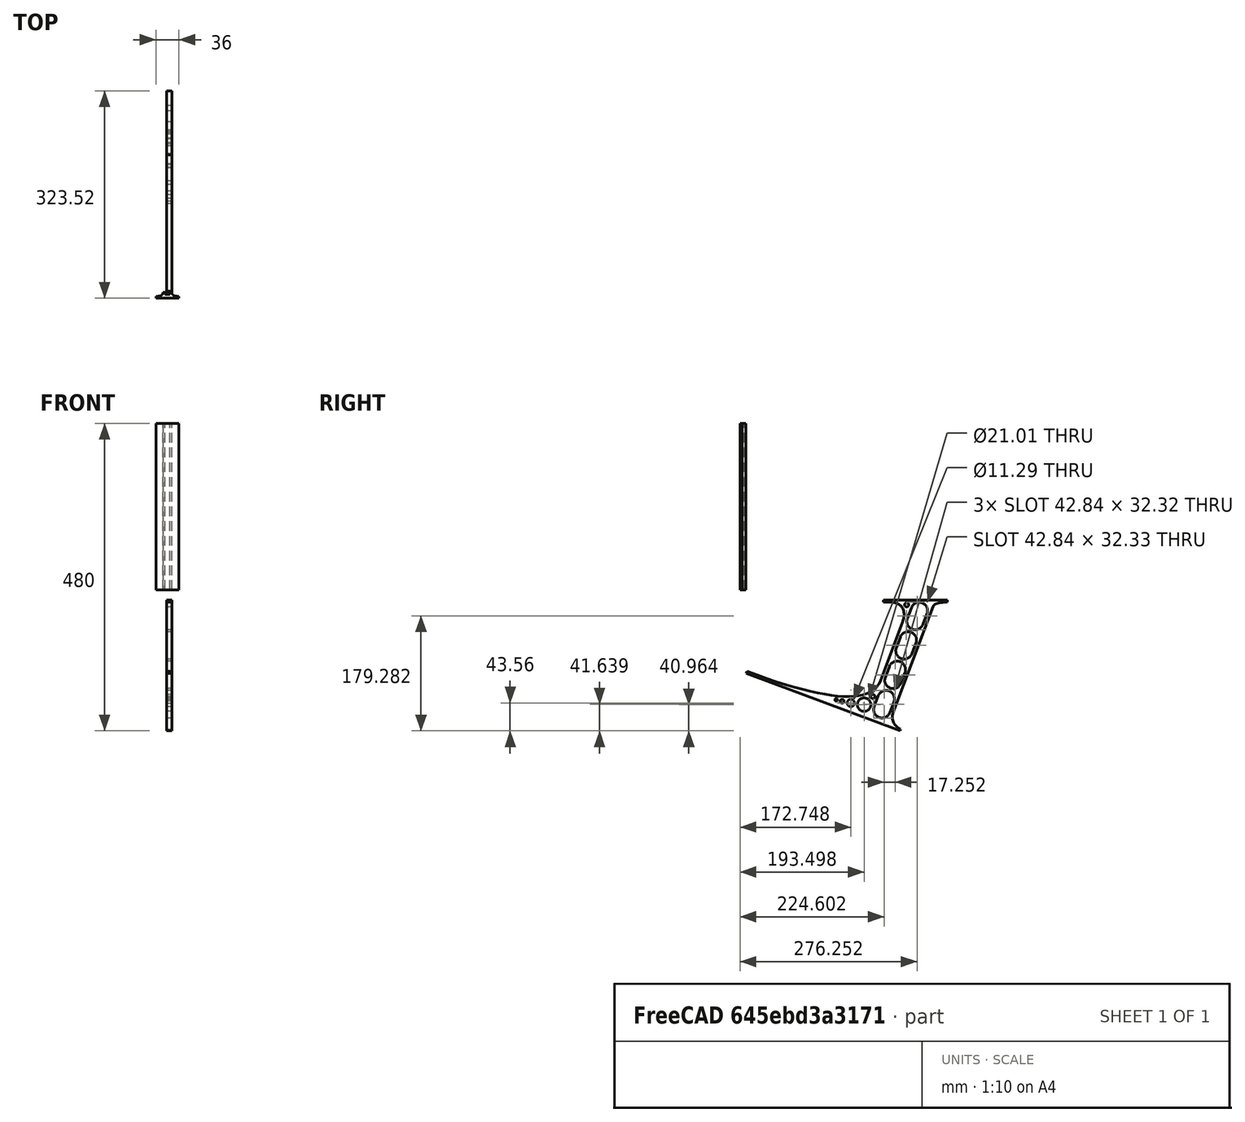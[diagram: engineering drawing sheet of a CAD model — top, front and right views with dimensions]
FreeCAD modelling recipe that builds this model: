
FCSTD DOCUMENT  (FreeCAD 0.19R0.19.2)
Label: laptopStand118FCStd
License: All rights reserved
LicenseURL: http://en.wikipedia.org/wiki/All_rights_reserved
objects: Sketcher::SketchObject×3, Part::Extrusion×3
note: 6 computed .brp shape members not serialized (recipe doc carries the construction recipe); baked Part::Feature solids carry a one-line shape summary decoded from their .brp

FEATURE [Sketcher::SketchObject] Sketch
  FullyConstrained = true
  sketch-geometry (329):
    g0: LineSegment StartX=-10.9272 StartY=-82.7794 StartZ=0 EndX=46.0728 EndY=-51.4823 EndZ=0
    g1: LineSegment StartX=-10.9272 StartY=77.3346 StartZ=0 EndX=-10.9272 EndY=-82.7794 EndZ=0
    g2: LineSegment StartX=-1.92719 StartY=-91.7794 StartZ=0 EndX=46.0728 EndY=-91.7794 EndZ=0
    g3: LineSegment StartX=46.0728 StartY=-65.424 StartZ=0 EndX=-1.92719 EndY=-91.7794 EndZ=0
    g4: LineSegment StartX=46.0728 StartY=-65.424 StartZ=0 EndX=46.0728 EndY=-91.7794 EndZ=0
    g5: LineSegment StartX=46.0728 StartY=77.3346 StartZ=0 EndX=46.0728 EndY=-51.4823 EndZ=0
    g6: LineSegment StartX=-42.9272 StartY=136.221 StartZ=0 EndX=-42.9272 EndY=-103.779 EndZ=0
    g7: LineSegment StartX=407.073 StartY=136.221 StartZ=0 EndX=407.073 EndY=-103.779 EndZ=0
    g8: ArcOfCircle CenterX=-26.9272 CenterY=22.1087 CenterZ=0 NormalX=0 NormalY=0 NormalZ=1 AngleXU=0 Radius=8 StartAngle=1e-16 EndAngle=3.14159
    g9: ArcOfCircle CenterX=-26.9272 CenterY=-83.7794 CenterZ=0 NormalX=0 NormalY=0 NormalZ=1 AngleXU=0 Radius=8 StartAngle=3.14159 EndAngle=6.28319
    g10: LineSegment StartX=-34.9272 StartY=22.1087 StartZ=0 EndX=-34.9272 EndY=-83.7794 EndZ=0
    g11: LineSegment StartX=-18.9272 StartY=22.1087 StartZ=0 EndX=-18.9272 EndY=-83.7794 EndZ=0
    g12: ArcOfCircle CenterX=391.073 CenterY=22.1087 CenterZ=0 NormalX=0 NormalY=0 NormalZ=1 AngleXU=0 Radius=8 StartAngle=-4.4e-15 EndAngle=3.14159
    g13: LineSegment StartX=399.073 StartY=22.1087 StartZ=0 EndX=399.073 EndY=-83.7794 EndZ=0
    g14: LineSegment StartX=383.073 StartY=22.1087 StartZ=0 EndX=383.073 EndY=-83.7794 EndZ=0
    g15: ArcOfCircle CenterX=391.073 CenterY=-83.7794 CenterZ=0 NormalX=0 NormalY=0 NormalZ=1 AngleXU=0 Radius=8 StartAngle=3.14159 EndAngle=6.28319
    g16: Circle CenterX=175.022 CenterY=27.0628 CenterZ=0 NormalX=0 NormalY=0 NormalZ=1 AngleXU=0 Radius=1
    g17: Circle CenterX=179.022 CenterY=24.8665 CenterZ=0 NormalX=0 NormalY=0 NormalZ=1 AngleXU=0 Radius=1
    g18: Circle CenterX=179.022 CenterY=27.0628 CenterZ=0 NormalX=0 NormalY=0 NormalZ=1 AngleXU=0 Radius=1
    g19: BSplineCurve PolesCount=3 KnotsCount=2 Degree=2 IsPeriodic=0
    g20: GeomPoint X=175.022 Y=27.0628 Z=0
    g21: GeomPoint X=179.022 Y=27.0628 Z=0
    g22: Circle CenterX=189.124 CenterY=27.0628 CenterZ=0 NormalX=0 NormalY=0 NormalZ=1 AngleXU=0 Radius=1
    g23: Circle CenterX=185.124 CenterY=24.8665 CenterZ=0 NormalX=0 NormalY=0 NormalZ=1 AngleXU=0 Radius=1
    g24: Circle CenterX=185.124 CenterY=27.0628 CenterZ=0 NormalX=0 NormalY=0 NormalZ=1 AngleXU=0 Radius=1
    g25: BSplineCurve PolesCount=3 KnotsCount=2 Degree=2 IsPeriodic=0
    g26: GeomPoint X=189.124 Y=27.0628 Z=0
    g27: GeomPoint X=185.124 Y=27.0628 Z=0
    g28: Circle CenterX=175.022 CenterY=5.37834 CenterZ=0 NormalX=0 NormalY=0 NormalZ=1 AngleXU=0 Radius=1
    g29: Circle CenterX=179.022 CenterY=7.57463 CenterZ=0 NormalX=0 NormalY=0 NormalZ=1 AngleXU=0 Radius=1
    g30: Circle CenterX=179.022 CenterY=5.34704 CenterZ=0 NormalX=0 NormalY=0 NormalZ=1 AngleXU=0 Radius=1
    g31: BSplineCurve PolesCount=3 KnotsCount=2 Degree=2 IsPeriodic=0
    g32: GeomPoint X=175.022 Y=5.37834 Z=0
    g33: GeomPoint X=179.022 Y=5.34704 Z=0
    g34: Circle CenterX=189.124 CenterY=5.37834 CenterZ=0 NormalX=0 NormalY=0 NormalZ=1 AngleXU=0 Radius=1
    g35: Circle CenterX=185.124 CenterY=7.57463 CenterZ=0 NormalX=0 NormalY=0 NormalZ=1 AngleXU=0 Radius=1
    g36: Circle CenterX=185.124 CenterY=5.34704 CenterZ=0 NormalX=0 NormalY=0 NormalZ=1 AngleXU=0 Radius=1
    g37: BSplineCurve PolesCount=3 KnotsCount=2 Degree=2 IsPeriodic=0
    g38: GeomPoint X=189.124 Y=5.37834 Z=0
    g39: GeomPoint X=185.124 Y=5.34704 Z=0
    g40: Circle CenterX=165.871 CenterY=18.1458 CenterZ=0 NormalX=0 NormalY=0 NormalZ=1 AngleXU=0 Radius=1
    g41: Circle CenterX=169.377 CenterY=16.2206 CenterZ=0 NormalX=0 NormalY=0 NormalZ=1 AngleXU=0 Radius=1
    g42: Circle CenterX=165.871 CenterY=14.2954 CenterZ=0 NormalX=0 NormalY=0 NormalZ=1 AngleXU=0 Radius=1
    g43: BSplineCurve PolesCount=3 KnotsCount=2 Degree=2 IsPeriodic=0
    g44: GeomPoint X=165.871 Y=18.1458 Z=0
    g45: GeomPoint X=165.871 Y=14.2954 Z=0
    g46: Circle CenterX=198.275 CenterY=18.1458 CenterZ=0 NormalX=0 NormalY=0 NormalZ=1 AngleXU=0 Radius=1
    g47: Circle CenterX=194.768 CenterY=16.2206 CenterZ=0 NormalX=0 NormalY=0 NormalZ=1 AngleXU=0 Radius=1
    g48: Circle CenterX=198.275 CenterY=14.2954 CenterZ=0 NormalX=0 NormalY=0 NormalZ=1 AngleXU=0 Radius=1
    g49: BSplineCurve PolesCount=3 KnotsCount=2 Degree=2 IsPeriodic=0
    g50: GeomPoint X=198.275 Y=18.1458 Z=0
    g51: GeomPoint X=198.275 Y=14.2954 Z=0
    g52: LineSegment StartX=407.073 StartY=-103.779 StartZ=0 EndX=-42.9272 EndY=-103.779 EndZ=0
    g53: LineSegment StartX=407.073 StartY=136.221 StartZ=0 EndX=-42.9272 EndY=136.221 EndZ=0
    g54: LineSegment StartX=46.0728 StartY=77.3346 StartZ=0 EndX=-10.9272 EndY=77.3346 EndZ=0
    g55: Circle CenterX=125.607 CenterY=54.1951 CenterZ=0 NormalX=0 NormalY=0 NormalZ=1 AngleXU=0 Radius=1
    g56: Circle CenterX=139.632 CenterY=46.4944 CenterZ=0 NormalX=0 NormalY=0 NormalZ=1 AngleXU=0 Radius=1
    g57: Circle CenterX=127.326 CenterY=56.7187 CenterZ=0 NormalX=0 NormalY=0 NormalZ=1 AngleXU=0 Radius=1
    g58: BSplineCurve PolesCount=3 KnotsCount=2 Degree=2 IsPeriodic=0
    g59: GeomPoint X=125.607 Y=54.1951 Z=0
    g60: GeomPoint X=127.326 Y=56.7187 Z=0
    g61: Circle CenterX=236.821 CenterY=56.7187 CenterZ=0 NormalX=0 NormalY=0 NormalZ=1 AngleXU=0 Radius=1
    g62: Circle CenterX=224.513 CenterY=46.4944 CenterZ=0 NormalX=0 NormalY=0 NormalZ=1 AngleXU=0 Radius=1
    g63: Circle CenterX=238.538 CenterY=54.1951 CenterZ=0 NormalX=0 NormalY=0 NormalZ=1 AngleXU=0 Radius=1
    g64: BSplineCurve PolesCount=3 KnotsCount=2 Degree=2 IsPeriodic=0
    g65: GeomPoint X=236.821 Y=56.7187 Z=0
    g66: GeomPoint X=238.538 Y=54.1951 Z=0
    g67: Circle CenterX=238.538 CenterY=-21.7539 CenterZ=0 NormalX=0 NormalY=0 NormalZ=1 AngleXU=0 Radius=1
    g68: Circle CenterX=224.513 CenterY=-14.0532 CenterZ=0 NormalX=0 NormalY=0 NormalZ=1 AngleXU=0 Radius=1
    g69: Circle CenterX=236.821 CenterY=-24.2775 CenterZ=0 NormalX=0 NormalY=0 NormalZ=1 AngleXU=0 Radius=1
    g70: BSplineCurve PolesCount=3 KnotsCount=2 Degree=2 IsPeriodic=0
    g71: GeomPoint X=238.538 Y=-21.7539 Z=0
    g72: GeomPoint X=236.821 Y=-24.2775 Z=0
    g73: Circle CenterX=125.607 CenterY=-21.7539 CenterZ=0 NormalX=0 NormalY=0 NormalZ=1 AngleXU=0 Radius=1
    g74: Circle CenterX=139.632 CenterY=-14.0532 CenterZ=0 NormalX=0 NormalY=0 NormalZ=1 AngleXU=0 Radius=1
    g75: Circle CenterX=127.325 CenterY=-24.2775 CenterZ=0 NormalX=0 NormalY=0 NormalZ=1 AngleXU=0 Radius=1
    g76: BSplineCurve PolesCount=3 KnotsCount=2 Degree=2 IsPeriodic=0
    g77: GeomPoint X=125.607 Y=-21.7539 Z=0
    g78: GeomPoint X=127.325 Y=-24.2775 Z=0
    g79: Circle CenterX=302.996 CenterY=111.695 CenterZ=0 NormalX=0 NormalY=0 NormalZ=1 AngleXU=0 Radius=1
    g80: Circle CenterX=306.073 CenterY=114.251 CenterZ=0 NormalX=0 NormalY=0 NormalZ=1 AngleXU=0 Radius=1
    g81: Circle CenterX=306.073 CenterY=110.251 CenterZ=0 NormalX=0 NormalY=0 NormalZ=1 AngleXU=0 Radius=1
    g82: BSplineCurve PolesCount=3 KnotsCount=2 Degree=2 IsPeriodic=0
    g83: GeomPoint X=302.996 Y=111.695 Z=0
    g84: GeomPoint X=306.073 Y=110.251 Z=0
    g85: Circle CenterX=306.073 CenterY=95.2763 CenterZ=0 NormalX=0 NormalY=0 NormalZ=1 AngleXU=0 Radius=1
    g86: Circle CenterX=306.073 CenterY=91.2763 CenterZ=0 NormalX=0 NormalY=0 NormalZ=1 AngleXU=0 Radius=1
    g87: Circle CenterX=302.567 CenterY=89.3511 CenterZ=0 NormalX=0 NormalY=0 NormalZ=1 AngleXU=0 Radius=1
    g88: BSplineCurve PolesCount=3 KnotsCount=2 Degree=2 IsPeriodic=0
    g89: GeomPoint X=306.073 Y=95.2763 Z=0
    g90: GeomPoint X=302.567 Y=89.3511 Z=0
    g91: LineSegment StartX=306.073 StartY=110.251 StartZ=0 EndX=306.073 EndY=95.2763 EndZ=0
    g92: LineSegment StartX=302.996 StartY=111.695 StartZ=0 EndX=236.821 EndY=56.7187 EndZ=0
    g93: LineSegment StartX=238.538 StartY=54.1951 StartZ=0 EndX=302.567 EndY=89.3511 EndZ=0
    g94: Circle CenterX=61.1496 CenterY=111.695 CenterZ=0 NormalX=0 NormalY=0 NormalZ=1 AngleXU=0 Radius=1
    g95: Circle CenterX=58.0728 CenterY=114.251 CenterZ=0 NormalX=0 NormalY=0 NormalZ=1 AngleXU=0 Radius=1
    g96: Circle CenterX=58.0728 CenterY=110.251 CenterZ=0 NormalX=0 NormalY=0 NormalZ=1 AngleXU=0 Radius=1
    g97: BSplineCurve PolesCount=3 KnotsCount=2 Degree=2 IsPeriodic=0
    g98: GeomPoint X=61.1496 Y=111.695 Z=0
    g99: GeomPoint X=58.0728 Y=110.251 Z=0
    g100: Circle CenterX=61.5791 CenterY=89.3511 CenterZ=0 NormalX=0 NormalY=0 NormalZ=1 AngleXU=0 Radius=1
    g101: Circle CenterX=58.0728 CenterY=91.2763 CenterZ=0 NormalX=0 NormalY=0 NormalZ=1 AngleXU=0 Radius=1
    g102: Circle CenterX=58.0728 CenterY=95.2763 CenterZ=0 NormalX=0 NormalY=0 NormalZ=1 AngleXU=0 Radius=1
    g103: BSplineCurve PolesCount=3 KnotsCount=2 Degree=2 IsPeriodic=0
    g104: GeomPoint X=61.5791 Y=89.3511 Z=0
    g105: GeomPoint X=58.0728 Y=95.2763 Z=0
    g106: LineSegment StartX=58.0728 StartY=110.251 StartZ=0 EndX=58.0728 EndY=95.2763 EndZ=0
    g107: LineSegment StartX=61.1496 StartY=111.695 StartZ=0 EndX=127.326 EndY=56.7187 EndZ=0
    g108: LineSegment StartX=125.607 StartY=54.1951 StartZ=0 EndX=61.5791 EndY=89.3511 EndZ=0
    g109: Circle CenterX=61.5791 CenterY=-56.9099 CenterZ=0 NormalX=0 NormalY=0 NormalZ=1 AngleXU=0 Radius=1
    g110: Circle CenterX=58.0728 CenterY=-58.8351 CenterZ=0 NormalX=0 NormalY=0 NormalZ=1 AngleXU=0 Radius=1
    g111: Circle CenterX=58.0728 CenterY=-62.8351 CenterZ=0 NormalX=0 NormalY=0 NormalZ=1 AngleXU=0 Radius=1
    g112: BSplineCurve PolesCount=3 KnotsCount=2 Degree=2 IsPeriodic=0
    g113: GeomPoint X=61.5791 Y=-56.9099 Z=0
    g114: GeomPoint X=58.0728 Y=-62.8351 Z=0
    g115: Circle CenterX=58.0728 CenterY=-77.8102 CenterZ=0 NormalX=0 NormalY=0 NormalZ=1 AngleXU=0 Radius=1
    g116: Circle CenterX=58.0728 CenterY=-81.8102 CenterZ=0 NormalX=0 NormalY=0 NormalZ=1 AngleXU=0 Radius=1
    g117: Circle CenterX=61.1496 CenterY=-79.2541 CenterZ=0 NormalX=0 NormalY=0 NormalZ=1 AngleXU=0 Radius=1
    g118: BSplineCurve PolesCount=3 KnotsCount=2 Degree=2 IsPeriodic=0
    g119: GeomPoint X=58.0728 Y=-77.8102 Z=0
    g120: GeomPoint X=61.1496 Y=-79.2541 Z=0
    g121: LineSegment StartX=58.0728 StartY=-62.8351 StartZ=0 EndX=58.0728 EndY=-77.8102 EndZ=0
    g122: LineSegment StartX=61.1496 StartY=-79.2541 StartZ=0 EndX=127.325 EndY=-24.2775 EndZ=0
    g123: LineSegment StartX=125.607 StartY=-21.7539 StartZ=0 EndX=61.5791 EndY=-56.9099 EndZ=0
    g124: Circle CenterX=302.567 CenterY=-56.9099 CenterZ=0 NormalX=0 NormalY=0 NormalZ=1 AngleXU=0 Radius=1
    g125: Circle CenterX=306.073 CenterY=-58.8351 CenterZ=0 NormalX=0 NormalY=0 NormalZ=1 AngleXU=0 Radius=1
    g126: Circle CenterX=306.073 CenterY=-62.8351 CenterZ=0 NormalX=0 NormalY=0 NormalZ=1 AngleXU=0 Radius=1
    g127: BSplineCurve PolesCount=3 KnotsCount=2 Degree=2 IsPeriodic=0
    g128: GeomPoint X=302.567 Y=-56.9099 Z=0
    g129: GeomPoint X=306.073 Y=-62.8351 Z=0
    g130: Circle CenterX=302.996 CenterY=-79.2541 CenterZ=0 NormalX=0 NormalY=0 NormalZ=1 AngleXU=0 Radius=1
    g131: Circle CenterX=306.073 CenterY=-81.8102 CenterZ=0 NormalX=0 NormalY=0 NormalZ=1 AngleXU=0 Radius=1
    g132: Circle CenterX=306.073 CenterY=-77.8102 CenterZ=0 NormalX=0 NormalY=0 NormalZ=1 AngleXU=0 Radius=1
    g133: BSplineCurve PolesCount=3 KnotsCount=2 Degree=2 IsPeriodic=0
    g134: GeomPoint X=302.996 Y=-79.2541 Z=0
    g135: GeomPoint X=306.073 Y=-77.8102 Z=0
    g136: LineSegment StartX=306.073 StartY=-62.8351 StartZ=0 EndX=306.073 EndY=-77.8102 EndZ=0
    g137: LineSegment StartX=302.996 StartY=-79.2541 StartZ=0 EndX=236.821 EndY=-24.2775 EndZ=0
    g138: LineSegment StartX=238.538 StartY=-21.7539 StartZ=0 EndX=302.567 EndY=-56.9099 EndZ=0
    g139: Circle CenterX=61.6457 CenterY=-88.8112 CenterZ=0 NormalX=0 NormalY=0 NormalZ=1 AngleXU=0 Radius=1
    g140: Circle CenterX=58.0728 CenterY=-91.7794 CenterZ=0 NormalX=0 NormalY=0 NormalZ=1 AngleXU=0 Radius=1
    g141: Circle CenterX=63.9135 CenterY=-91.7794 CenterZ=0 NormalX=0 NormalY=0 NormalZ=1 AngleXU=0 Radius=1
    g142: BSplineCurve PolesCount=3 KnotsCount=2 Degree=2 IsPeriodic=0
    g143: GeomPoint X=61.6457 Y=-88.8112 Z=0
    g144: GeomPoint X=63.9135 Y=-91.7794 Z=0
    g145: Circle CenterX=179.022 CenterY=-85.8163 CenterZ=0 NormalX=0 NormalY=0 NormalZ=1 AngleXU=0 Radius=1
    g146: Circle CenterX=179.022 CenterY=-91.7794 CenterZ=0 NormalX=0 NormalY=0 NormalZ=1 AngleXU=0 Radius=1
    g147: Circle CenterX=171.895 CenterY=-91.7794 CenterZ=0 NormalX=0 NormalY=0 NormalZ=1 AngleXU=0 Radius=1
    g148: BSplineCurve PolesCount=3 KnotsCount=2 Degree=2 IsPeriodic=0
    g149: GeomPoint X=179.022 Y=-85.8163 Z=0
    g150: GeomPoint X=171.895 Y=-91.7794 Z=0
    g151: Circle CenterX=185.124 CenterY=-86.2028 CenterZ=0 NormalX=0 NormalY=0 NormalZ=1 AngleXU=0 Radius=1
    g152: Circle CenterX=185.124 CenterY=-91.7794 CenterZ=0 NormalX=0 NormalY=0 NormalZ=1 AngleXU=0 Radius=1
    g153: Circle CenterX=191.747 CenterY=-91.7794 CenterZ=0 NormalX=0 NormalY=0 NormalZ=1 AngleXU=0 Radius=1
    g154: BSplineCurve PolesCount=3 KnotsCount=2 Degree=2 IsPeriodic=0
    g155: GeomPoint X=185.124 Y=-86.2028 Z=0
    g156: GeomPoint X=191.747 Y=-91.7794 Z=0
    g157: Circle CenterX=299.888 CenterY=-86.6413 CenterZ=0 NormalX=0 NormalY=0 NormalZ=1 AngleXU=0 Radius=1
    g158: Circle CenterX=306.073 CenterY=-91.7794 CenterZ=0 NormalX=0 NormalY=0 NormalZ=1 AngleXU=0 Radius=1
    g159: Circle CenterX=298.776 CenterY=-91.7794 CenterZ=0 NormalX=0 NormalY=0 NormalZ=1 AngleXU=0 Radius=1
    g160: BSplineCurve PolesCount=3 KnotsCount=2 Degree=2 IsPeriodic=0
    g161: GeomPoint X=299.888 Y=-86.6413 Z=0
    g162: GeomPoint X=298.776 Y=-91.7794 Z=0
    g163: LineSegment StartX=189.124 StartY=5.37834 StartZ=0 EndX=299.888 EndY=-86.6413 EndZ=0
    g164: LineSegment StartX=298.776 StartY=-91.7794 StartZ=0 EndX=191.747 EndY=-91.7794 EndZ=0
    g165: LineSegment StartX=185.124 StartY=-86.2028 StartZ=0 EndX=185.124 EndY=5.34704 EndZ=0
    g166: LineSegment StartX=179.022 StartY=5.34704 StartZ=0 EndX=179.022 EndY=-85.8163 EndZ=0
    g167: LineSegment StartX=171.895 StartY=-91.7794 StartZ=0 EndX=63.9135 EndY=-91.7794 EndZ=0
    g168: LineSegment StartX=61.6457 StartY=-88.8112 StartZ=0 EndX=175.022 EndY=5.37834 EndZ=0
    g169: Circle CenterX=302.073 CenterY=124.221 CenterZ=0 NormalX=0 NormalY=0 NormalZ=1 AngleXU=0 Radius=1
    g170: Circle CenterX=306.073 CenterY=124.221 CenterZ=0 NormalX=0 NormalY=0 NormalZ=1 AngleXU=0 Radius=1
    g171: Circle CenterX=302.996 CenterY=121.665 CenterZ=0 NormalX=0 NormalY=0 NormalZ=1 AngleXU=0 Radius=1
    g172: BSplineCurve PolesCount=3 KnotsCount=2 Degree=2 IsPeriodic=0
    g173: GeomPoint X=302.073 Y=124.221 Z=0
    g174: GeomPoint X=302.996 Y=121.665 Z=0
    g175: Circle CenterX=189.124 CenterY=124.221 CenterZ=0 NormalX=0 NormalY=0 NormalZ=1 AngleXU=0 Radius=1
    g176: Circle CenterX=185.124 CenterY=124.221 CenterZ=0 NormalX=0 NormalY=0 NormalZ=1 AngleXU=0 Radius=1
    g177: Circle CenterX=185.124 CenterY=120.221 CenterZ=0 NormalX=0 NormalY=0 NormalZ=1 AngleXU=0 Radius=1
    g178: BSplineCurve PolesCount=3 KnotsCount=2 Degree=2 IsPeriodic=0
    g179: GeomPoint X=189.124 Y=124.221 Z=0
    g180: GeomPoint X=185.124 Y=120.221 Z=0
    g181: Circle CenterX=175.022 CenterY=124.221 CenterZ=0 NormalX=0 NormalY=0 NormalZ=1 AngleXU=0 Radius=1
    g182: Circle CenterX=179.022 CenterY=124.221 CenterZ=0 NormalX=0 NormalY=0 NormalZ=1 AngleXU=0 Radius=1
    g183: Circle CenterX=179.022 CenterY=120.221 CenterZ=0 NormalX=0 NormalY=0 NormalZ=1 AngleXU=0 Radius=1
    g184: BSplineCurve PolesCount=3 KnotsCount=2 Degree=2 IsPeriodic=0
    g185: GeomPoint X=175.022 Y=124.221 Z=0
    g186: GeomPoint X=179.022 Y=120.221 Z=0
    g187: Circle CenterX=62.0728 CenterY=124.221 CenterZ=0 NormalX=0 NormalY=0 NormalZ=1 AngleXU=0 Radius=1
    g188: Circle CenterX=58.0728 CenterY=124.221 CenterZ=0 NormalX=0 NormalY=0 NormalZ=1 AngleXU=0 Radius=1
    g189: Circle CenterX=61.1496 CenterY=121.665 CenterZ=0 NormalX=0 NormalY=0 NormalZ=1 AngleXU=0 Radius=1
    g190: BSplineCurve PolesCount=3 KnotsCount=2 Degree=2 IsPeriodic=0
    g191: GeomPoint X=62.0728 Y=124.221 Z=0
    g192: GeomPoint X=61.1496 Y=121.665 Z=0
    g193: LineSegment StartX=62.0728 StartY=124.221 StartZ=0 EndX=175.022 EndY=124.221 EndZ=0
    g194: LineSegment StartX=179.022 StartY=120.221 StartZ=0 EndX=179.022 EndY=27.0628 EndZ=0
    g195: LineSegment StartX=185.124 StartY=27.0628 StartZ=0 EndX=185.124 EndY=120.221 EndZ=0
    g196: LineSegment StartX=189.124 StartY=124.221 StartZ=0 EndX=302.073 EndY=124.221 EndZ=0
    g197: LineSegment StartX=302.996 StartY=121.665 StartZ=0 EndX=189.124 EndY=27.0628 EndZ=0
    g198: LineSegment StartX=175.022 StartY=27.0628 StartZ=0 EndX=61.1496 EndY=121.665 EndZ=0
    g199: Circle CenterX=61.5791 CenterY=75.4095 CenterZ=0 NormalX=0 NormalY=0 NormalZ=1 AngleXU=0 Radius=1
    g200: Circle CenterX=58.0728 CenterY=77.3346 CenterZ=0 NormalX=0 NormalY=0 NormalZ=1 AngleXU=0 Radius=1
    g201: Circle CenterX=58.0728 CenterY=73.3346 CenterZ=0 NormalX=0 NormalY=0 NormalZ=1 AngleXU=0 Radius=1
    g202: BSplineCurve PolesCount=3 KnotsCount=2 Degree=2 IsPeriodic=0
    g203: GeomPoint X=61.5791 Y=75.4095 Z=0
    g204: GeomPoint X=58.0728 Y=73.3346 Z=0
    g205: Circle CenterX=58.0728 CenterY=-40.8935 CenterZ=0 NormalX=0 NormalY=0 NormalZ=1 AngleXU=0 Radius=1
    g206: Circle CenterX=58.0728 CenterY=-44.8935 CenterZ=0 NormalX=0 NormalY=0 NormalZ=1 AngleXU=0 Radius=1
    g207: Circle CenterX=61.5791 CenterY=-42.9683 CenterZ=0 NormalX=0 NormalY=0 NormalZ=1 AngleXU=0 Radius=1
    g208: BSplineCurve PolesCount=3 KnotsCount=2 Degree=2 IsPeriodic=0
    g209: GeomPoint X=58.0728 Y=-40.8935 Z=0
    g210: GeomPoint X=61.5791 Y=-42.9683 Z=0
    g211: LineSegment StartX=61.5791 StartY=-42.9683 StartZ=0 EndX=165.871 EndY=14.2954 EndZ=0
    g212: LineSegment StartX=165.871 StartY=18.1458 StartZ=0 EndX=61.5791 EndY=75.4095 EndZ=0
    g213: LineSegment StartX=58.0728 StartY=73.3346 StartZ=0 EndX=58.0728 EndY=-40.8935 EndZ=0
    g214: Circle CenterX=302.567 CenterY=-42.9683 CenterZ=0 NormalX=0 NormalY=0 NormalZ=1 AngleXU=0 Radius=1
    g215: Circle CenterX=306.073 CenterY=-44.8935 CenterZ=0 NormalX=0 NormalY=0 NormalZ=1 AngleXU=0 Radius=1
    g216: Circle CenterX=306.073 CenterY=-40.8935 CenterZ=0 NormalX=0 NormalY=0 NormalZ=1 AngleXU=0 Radius=1
    g217: BSplineCurve PolesCount=3 KnotsCount=2 Degree=2 IsPeriodic=0
    g218: GeomPoint X=302.567 Y=-42.9683 Z=0
    g219: GeomPoint X=306.073 Y=-40.8935 Z=0
    g220: Circle CenterX=306.073 CenterY=73.3346 CenterZ=0 NormalX=0 NormalY=0 NormalZ=1 AngleXU=0 Radius=1
    g221: Circle CenterX=306.073 CenterY=77.3346 CenterZ=0 NormalX=0 NormalY=0 NormalZ=1 AngleXU=0 Radius=1
    g222: Circle CenterX=302.567 CenterY=75.4095 CenterZ=0 NormalX=0 NormalY=0 NormalZ=1 AngleXU=0 Radius=1
    g223: BSplineCurve PolesCount=3 KnotsCount=2 Degree=2 IsPeriodic=0
    g224: GeomPoint X=306.073 Y=73.3346 Z=0
    g225: GeomPoint X=302.567 Y=75.4095 Z=0
    g226: LineSegment StartX=302.567 StartY=-42.9683 StartZ=0 EndX=198.275 EndY=14.2954 EndZ=0
    g227: LineSegment StartX=198.275 StartY=18.1458 StartZ=0 EndX=302.567 EndY=75.4095 EndZ=0
    g228: LineSegment StartX=306.073 StartY=73.3346 StartZ=0 EndX=306.073 EndY=-40.8935 EndZ=0
    g229: LineSegment StartX=322.073 StartY=105.865 StartZ=0 EndX=328.643 EndY=105.865 EndZ=0
    g230: LineSegment StartX=318.073 StartY=120.221 StartZ=0 EndX=318.073 EndY=109.865 EndZ=0
    g231: LineSegment StartX=336.157 StartY=107.779 StartZ=0 EndX=362.567 EndY=122.294 EndZ=0
    g232: Circle CenterX=362.073 CenterY=124.221 CenterZ=0 NormalX=0 NormalY=0 NormalZ=1 AngleXU=0 Radius=1
    g233: Circle CenterX=366.073 CenterY=124.221 CenterZ=0 NormalX=0 NormalY=0 NormalZ=1 AngleXU=0 Radius=1
    g234: Circle CenterX=362.567 CenterY=122.294 CenterZ=0 NormalX=0 NormalY=0 NormalZ=1 AngleXU=0 Radius=1
    g235: BSplineCurve PolesCount=3 KnotsCount=2 Degree=2 IsPeriodic=0
    g236: GeomPoint X=362.073 Y=124.221 Z=0
    g237: GeomPoint X=362.567 Y=122.294 Z=0
    g238: Circle CenterX=322.073 CenterY=124.221 CenterZ=0 NormalX=0 NormalY=0 NormalZ=1 AngleXU=0 Radius=1
    g239: Circle CenterX=318.073 CenterY=124.221 CenterZ=0 NormalX=0 NormalY=0 NormalZ=1 AngleXU=0 Radius=1
    g240: Circle CenterX=318.073 CenterY=120.221 CenterZ=0 NormalX=0 NormalY=0 NormalZ=1 AngleXU=0 Radius=1
    g241: BSplineCurve PolesCount=3 KnotsCount=2 Degree=2 IsPeriodic=0
    g242: GeomPoint X=322.073 Y=124.221 Z=0
    g243: GeomPoint X=318.073 Y=120.221 Z=0
    g244: Circle CenterX=322.073 CenterY=105.865 CenterZ=0 NormalX=0 NormalY=0 NormalZ=1 AngleXU=0 Radius=1
    g245: Circle CenterX=318.073 CenterY=105.865 CenterZ=0 NormalX=0 NormalY=0 NormalZ=1 AngleXU=0 Radius=1
    g246: Circle CenterX=318.073 CenterY=109.865 CenterZ=0 NormalX=0 NormalY=0 NormalZ=1 AngleXU=0 Radius=1
    g247: BSplineCurve PolesCount=3 KnotsCount=2 Degree=2 IsPeriodic=0
    g248: GeomPoint X=322.073 Y=105.865 Z=0
    g249: GeomPoint X=318.073 Y=109.865 Z=0
    g250: Circle CenterX=336.157 CenterY=107.779 CenterZ=0 NormalX=0 NormalY=0 NormalZ=1 AngleXU=0 Radius=1
    g251: Circle CenterX=332.651 CenterY=105.853 CenterZ=0 NormalX=0 NormalY=0 NormalZ=1 AngleXU=0 Radius=1
    g252: Circle CenterX=328.643 CenterY=105.865 CenterZ=0 NormalX=0 NormalY=0 NormalZ=1 AngleXU=0 Radius=1
    g253: BSplineCurve PolesCount=3 KnotsCount=2 Degree=2 IsPeriodic=0
    g254: GeomPoint X=336.157 Y=107.779 Z=0
    g255: GeomPoint X=328.643 Y=105.865 Z=0
    g256: LineSegment StartX=322.073 StartY=124.221 StartZ=0 EndX=362.073 EndY=124.221 EndZ=0
    g257: Circle CenterX=371.567 CenterY=-80.8644 CenterZ=0 NormalX=0 NormalY=0 NormalZ=1 AngleXU=0 Radius=1
    g258: Circle CenterX=375.073 CenterY=-82.7896 CenterZ=0 NormalX=0 NormalY=0 NormalZ=1 AngleXU=0 Radius=1
    g259: Circle CenterX=375.073 CenterY=-78.7896 CenterZ=0 NormalX=0 NormalY=0 NormalZ=1 AngleXU=0 Radius=1
    g260: BSplineCurve PolesCount=3 KnotsCount=2 Degree=2 IsPeriodic=0
    g261: GeomPoint X=371.567 Y=-80.8644 Z=0
    g262: GeomPoint X=375.073 Y=-78.7896 Z=0
    g263: Circle CenterX=321.579 CenterY=-53.4075 CenterZ=0 NormalX=0 NormalY=0 NormalZ=1 AngleXU=0 Radius=1
    g264: Circle CenterX=318.073 CenterY=-51.4823 CenterZ=0 NormalX=0 NormalY=0 NormalZ=1 AngleXU=0 Radius=1
    g265: Circle CenterX=318.073 CenterY=-47.4823 CenterZ=0 NormalX=0 NormalY=0 NormalZ=1 AngleXU=0 Radius=1
    g266: BSplineCurve PolesCount=3 KnotsCount=2 Degree=2 IsPeriodic=0
    g267: GeomPoint X=321.579 Y=-53.4075 Z=0
    g268: GeomPoint X=318.073 Y=-47.4823 Z=0
    g269: Circle CenterX=318.073 CenterY=79.9235 CenterZ=0 NormalX=0 NormalY=0 NormalZ=1 AngleXU=0 Radius=1
    g270: Circle CenterX=318.073 CenterY=83.9235 CenterZ=0 NormalX=0 NormalY=0 NormalZ=1 AngleXU=0 Radius=1
    g271: Circle CenterX=322.073 CenterY=83.9235 CenterZ=0 NormalX=0 NormalY=0 NormalZ=1 AngleXU=0 Radius=1
    g272: BSplineCurve PolesCount=3 KnotsCount=2 Degree=2 IsPeriodic=0
    g273: GeomPoint X=318.073 Y=79.9235 Z=0
    g274: GeomPoint X=322.073 Y=83.9235 Z=0
    g275: Circle CenterX=375.073 CenterY=79.9235 CenterZ=0 NormalX=0 NormalY=0 NormalZ=1 AngleXU=0 Radius=1
    g276: Circle CenterX=375.073 CenterY=83.9235 CenterZ=0 NormalX=0 NormalY=0 NormalZ=1 AngleXU=0 Radius=1
    g277: Circle CenterX=371.073 CenterY=83.9235 CenterZ=0 NormalX=0 NormalY=0 NormalZ=1 AngleXU=0 Radius=1
    g278: BSplineCurve PolesCount=3 KnotsCount=2 Degree=2 IsPeriodic=0
    g279: GeomPoint X=375.073 Y=79.9235 Z=0
    g280: GeomPoint X=371.073 Y=83.9235 Z=0
    g281: LineSegment StartX=322.073 StartY=83.9235 StartZ=0 EndX=371.073 EndY=83.9235 EndZ=0
    g282: LineSegment StartX=375.073 StartY=79.9235 StartZ=0 EndX=375.073 EndY=-78.7896 EndZ=0
    g283: LineSegment StartX=371.567 StartY=-80.8644 StartZ=0 EndX=321.579 EndY=-53.4075 EndZ=0
    g284: LineSegment StartX=318.073 StartY=-47.4823 StartZ=0 EndX=318.073 EndY=79.9235 EndZ=0
    g285: Circle CenterX=321.579 CenterY=-67.3492 CenterZ=0 NormalX=0 NormalY=0 NormalZ=1 AngleXU=0 Radius=1
    g286: Circle CenterX=318.073 CenterY=-65.424 CenterZ=0 NormalX=0 NormalY=0 NormalZ=1 AngleXU=0 Radius=1
    g287: Circle CenterX=318.073 CenterY=-69.424 CenterZ=0 NormalX=0 NormalY=0 NormalZ=1 AngleXU=0 Radius=1
    g288: BSplineCurve PolesCount=3 KnotsCount=2 Degree=2 IsPeriodic=0
    g289: GeomPoint X=321.579 Y=-67.3492 Z=0
    g290: GeomPoint X=318.073 Y=-69.424 Z=0
    g291: Circle CenterX=362.567 CenterY=-89.8542 CenterZ=0 NormalX=0 NormalY=0 NormalZ=1 AngleXU=0 Radius=1
    g292: Circle CenterX=366.073 CenterY=-91.7794 CenterZ=0 NormalX=0 NormalY=0 NormalZ=1 AngleXU=0 Radius=1
    g293: Circle CenterX=362.073 CenterY=-91.7794 CenterZ=0 NormalX=0 NormalY=0 NormalZ=1 AngleXU=0 Radius=1
    g294: BSplineCurve PolesCount=3 KnotsCount=2 Degree=2 IsPeriodic=0
    g295: GeomPoint X=362.567 Y=-89.8542 Z=0
    g296: GeomPoint X=362.073 Y=-91.7794 Z=0
    g297: Circle CenterX=322.073 CenterY=-91.7794 CenterZ=0 NormalX=0 NormalY=0 NormalZ=1 AngleXU=0 Radius=1
    g298: Circle CenterX=318.073 CenterY=-91.7794 CenterZ=0 NormalX=0 NormalY=0 NormalZ=1 AngleXU=0 Radius=1
    g299: Circle CenterX=318.073 CenterY=-87.7794 CenterZ=0 NormalX=0 NormalY=0 NormalZ=1 AngleXU=0 Radius=1
    g300: BSplineCurve PolesCount=3 KnotsCount=2 Degree=2 IsPeriodic=0
    g301: GeomPoint X=322.073 Y=-91.7794 Z=0
    g302: GeomPoint X=318.073 Y=-87.7794 Z=0
    g303: LineSegment StartX=362.567 StartY=-89.8542 StartZ=0 EndX=321.579 EndY=-67.3492 EndZ=0
    g304: LineSegment StartX=318.073 StartY=-69.424 StartZ=0 EndX=318.073 EndY=-87.7794 EndZ=0
    g305: LineSegment StartX=322.073 StartY=-91.7794 StartZ=0 EndX=362.073 EndY=-91.7794 EndZ=0
    g306: Circle CenterX=2.07281 CenterY=124.221 CenterZ=0 NormalX=0 NormalY=0 NormalZ=1 AngleXU=0 Radius=1
    g307: Circle CenterX=1.57905 CenterY=122.295 CenterZ=0 NormalX=0 NormalY=0 NormalZ=1 AngleXU=0 Radius=1
    g308: BSplineCurve PolesCount=3 KnotsCount=2 Degree=2 IsPeriodic=0
    g309: GeomPoint X=2.07281 Y=124.221 Z=0
    g310: GeomPoint X=1.57905 Y=122.295 Z=0
    g311: Circle CenterX=42.0728 CenterY=124.221 CenterZ=0 NormalX=0 NormalY=0 NormalZ=1 AngleXU=0 Radius=1
    g312: Circle CenterX=46.0728 CenterY=124.221 CenterZ=0 NormalX=0 NormalY=0 NormalZ=1 AngleXU=0 Radius=1
    g313: Circle CenterX=46.0728 CenterY=120.221 CenterZ=0 NormalX=0 NormalY=0 NormalZ=1 AngleXU=0 Radius=1
    g314: BSplineCurve PolesCount=3 KnotsCount=2 Degree=2 IsPeriodic=0
    g315: GeomPoint X=42.0728 Y=124.221 Z=0
    g316: GeomPoint X=46.0728 Y=120.221 Z=0
    g317: Circle CenterX=46.0728 CenterY=109.865 CenterZ=0 NormalX=0 NormalY=0 NormalZ=1 AngleXU=0 Radius=1
    g318: Circle CenterX=46.0728 CenterY=105.865 CenterZ=0 NormalX=0 NormalY=0 NormalZ=1 AngleXU=0 Radius=1
    g319: Circle CenterX=42.0728 CenterY=105.865 CenterZ=0 NormalX=0 NormalY=0 NormalZ=1 AngleXU=0 Radius=1
    g320: BSplineCurve PolesCount=3 KnotsCount=2 Degree=2 IsPeriodic=0
    g321: GeomPoint X=46.0728 Y=109.865 Z=0
    g322: GeomPoint X=42.0728 Y=105.865 Z=0
    g323: Circle CenterX=35.5028 CenterY=105.865 CenterZ=0 NormalX=0 NormalY=0 NormalZ=1 AngleXU=0 Radius=1
    g324: Circle CenterX=31.5028 CenterY=105.865 CenterZ=0 NormalX=0 NormalY=0 NormalZ=1 AngleXU=0 Radius=1
    g325: Circle CenterX=27.9965 CenterY=107.79 CenterZ=0 NormalX=0 NormalY=0 NormalZ=1 AngleXU=0 Radius=1
    g326: BSplineCurve PolesCount=3 KnotsCount=2 Degree=2 IsPeriodic=0
    g327: GeomPoint X=35.5028 Y=105.865 Z=0
    g328: GeomPoint X=27.9965 Y=107.79 Z=0
  constraints (541):
    c: Horizontal(g2)
    c: Coincident(g4,g3)
    c: Coincident(g0,g5)
    c: Block(g4)
    c: Block(g3)
    c: Block(g0)
    c: Block(g1)
    c: Block(g2)
    c: Vertical(g6)
    c: Vertical(g7)
    c: Block(g7)
    c: Block(g6)
    c: Tangent(g8,g11) = 1.5708
    c: Tangent(g8,g10) = -1.5708
    c: Tangent(g10,g9) = -1.5708
    c: Tangent(g11,g9) = 1.5708
    c: Vertical(g10)
    c: Equal(g8,g9)
    c: Block(g11)
    c: Block(g10)
    c: Tangent(g12,g13) = 1.5708
    c: Tangent(g13,g15) = 1.5708
    c: Equal(g12,g15)
    c: Coincident(g14,g12)
    c: Coincident(g14,g15)
    c: Block(g13)
    c: Block(g14)
    c: Weight(g16) = 1
    c: Equal(g16,g17)
    c: Equal(g16,g18)
    c: InternalAlignment(g16,g19)
    c: InternalAlignment(g17,g19)
    c: InternalAlignment(g18,g19)
    c: InternalAlignment(g20,g19)
    c: InternalAlignment(g21,g19)
    c: Weight(g22) = 1
    c: Equal(g22,g23)
    c: Equal(g22,g24)
    c: InternalAlignment(g22,g25)
    c: InternalAlignment(g23,g25)
    c: InternalAlignment(g24,g25)
    c: InternalAlignment(g26,g25)
    c: InternalAlignment(g27,g25)
    c: Block(g25)
    c: Block(g19)
    c: Weight(g28) = 1
    c: Equal(g28,g29)
    c: Equal(g28,g30)
    c: InternalAlignment(g28,g31)
    c: InternalAlignment(g29,g31)
    c: InternalAlignment(g30,g31)
    c: InternalAlignment(g32,g31)
    c: InternalAlignment(g33,g31)
    c: Weight(g34) = 1
    c: Equal(g34,g35)
    c: Equal(g34,g36)
    c: InternalAlignment(g34,g37)
    c: InternalAlignment(g35,g37)
    c: InternalAlignment(g36,g37)
    c: InternalAlignment(g38,g37)
    c: InternalAlignment(g39,g37)
    c: Block(g37)
    c: Block(g31)
    c: Weight(g40) = 1
    c: Equal(g40,g41)
    c: Equal(g40,g42)
    c: InternalAlignment(g40,g43)
    c: InternalAlignment(g41,g43)
    c: InternalAlignment(g42,g43)
    c: InternalAlignment(g44,g43)
    c: InternalAlignment(g45,g43)
    c: Weight(g46) = 1
    c: Equal(g46,g47)
    c: Equal(g46,g48)
    c: InternalAlignment(g46,g49)
    c: InternalAlignment(g47,g49)
    c: InternalAlignment(g48,g49)
    c: InternalAlignment(g50,g49)
    c: InternalAlignment(g51,g49)
    c: Block(g43)
    c: Block(g49)
    c: Coincident(g52,g7)
    c: Coincident(g52,g6)
    c: Horizontal(g52)
    c: Distance(g52) = 450
    c: Coincident(g53,g7)
    c: Coincident(g53,g6)
    c: Horizontal(g53)
    c: Horizontal(g54)
    c: Coincident(g5,g54)
    c: Block(g54)
    c: Coincident(g1,g54)
    c: Weight(g55) = 1
    c: Equal(g55,g56)
    c: Equal(g55,g57)
    c: InternalAlignment(g55,g58)
    c: InternalAlignment(g56,g58)
    c: InternalAlignment(g57,g58)
    c: InternalAlignment(g59,g58)
    c: InternalAlignment(g60,g58)
    c: Block(g58)
    c: Weight(g61) = 1
    c: Equal(g61,g62)
    c: Equal(g61,g63)
    c: InternalAlignment(g61,g64)
    c: InternalAlignment(g62,g64)
    c: InternalAlignment(g63,g64)
    c: InternalAlignment(g65,g64)
    c: InternalAlignment(g66,g64)
    c: Block(g64)
    c: Weight(g67) = 1
    c: Equal(g67,g68)
    c: Equal(g67,g69)
    c: InternalAlignment(g67,g70)
    c: InternalAlignment(g68,g70)
    c: InternalAlignment(g69,g70)
    c: InternalAlignment(g71,g70)
    c: InternalAlignment(g72,g70)
    c: Block(g70)
    c: Weight(g73) = 1
    c: Equal(g73,g74)
    c: Equal(g73,g75)
    c: InternalAlignment(g73,g76)
    c: InternalAlignment(g74,g76)
    c: InternalAlignment(g75,g76)
    c: InternalAlignment(g77,g76)
    c: InternalAlignment(g78,g76)
    c: Block(g76)
    c: Weight(g79) = 1
    c: Equal(g79,g80)
    c: Equal(g79,g81)
    c: InternalAlignment(g79,g82)
    c: InternalAlignment(g80,g82)
    c: InternalAlignment(g81,g82)
    c: InternalAlignment(g83,g82)
    c: InternalAlignment(g84,g82)
    c: Weight(g85) = 1
    c: Equal(g85,g86)
    c: Equal(g85,g87)
    c: InternalAlignment(g85,g88)
    c: InternalAlignment(g86,g88)
    c: InternalAlignment(g87,g88)
    c: InternalAlignment(g89,g88)
    c: InternalAlignment(g90,g88)
    c: Block(g82)
    c: Block(g88)
    c: Coincident(g91,g82)
    c: Coincident(g91,g88)
    c: Vertical(g91)
    c: Coincident(g92,g82)
    c: Coincident(g92,g64)
    c: Coincident(g93,g64)
    c: Coincident(g93,g88)
    c: Weight(g94) = 1
    c: Equal(g94,g95)
    c: Equal(g94,g96)
    c: InternalAlignment(g94,g97)
    c: InternalAlignment(g95,g97)
    c: InternalAlignment(g96,g97)
    c: InternalAlignment(g98,g97)
    c: InternalAlignment(g99,g97)
    c: Weight(g100) = 1
    c: Equal(g100,g101)
    c: Equal(g100,g102)
    c: InternalAlignment(g100,g103)
    c: InternalAlignment(g101,g103)
    c: InternalAlignment(g102,g103)
    c: InternalAlignment(g104,g103)
    c: InternalAlignment(g105,g103)
    c: Block(g97)
    c: Block(g103)
    c: Coincident(g106,g97)
    c: Coincident(g106,g103)
    c: Vertical(g106)
    c: Coincident(g107,g97)
    c: Coincident(g107,g58)
    c: Coincident(g108,g58)
    c: Coincident(g108,g103)
    c: Weight(g109) = 1
    c: Equal(g109,g110)
    c: Equal(g109,g111)
    c: InternalAlignment(g109,g112)
    c: InternalAlignment(g110,g112)
    c: InternalAlignment(g111,g112)
    c: InternalAlignment(g113,g112)
    c: InternalAlignment(g114,g112)
    c: Weight(g115) = 1
    c: Equal(g115,g116)
    c: Equal(g115,g117)
    c: InternalAlignment(g115,g118)
    c: InternalAlignment(g116,g118)
    c: InternalAlignment(g117,g118)
    c: InternalAlignment(g119,g118)
    c: InternalAlignment(g120,g118)
    c: Block(g112)
    c: Block(g118)
    c: Coincident(g121,g112)
    c: Coincident(g121,g118)
    c: Vertical(g121)
    c: Coincident(g122,g118)
    c: Coincident(g122,g76)
    c: Coincident(g123,g76)
    c: Coincident(g123,g112)
    c: Weight(g124) = 1
    c: Equal(g124,g125)
    c: Equal(g124,g126)
    c: InternalAlignment(g124,g127)
    c: InternalAlignment(g125,g127)
    c: InternalAlignment(g126,g127)
    c: InternalAlignment(g128,g127)
    c: InternalAlignment(g129,g127)
    c: Weight(g130) = 1
    c: Equal(g130,g131)
    c: Equal(g130,g132)
    c: InternalAlignment(g130,g133)
    c: InternalAlignment(g131,g133)
    c: InternalAlignment(g132,g133)
    c: InternalAlignment(g134,g133)
    c: InternalAlignment(g135,g133)
    c: Block(g127)
    c: Block(g133)
    c: Coincident(g136,g127)
    c: Coincident(g136,g133)
    c: Vertical(g136)
    c: Coincident(g137,g133)
    c: Coincident(g137,g70)
    c: Coincident(g138,g70)
    c: Coincident(g138,g127)
    c: Weight(g139) = 1
    c: Equal(g139,g140)
    c: Equal(g139,g141)
    c: InternalAlignment(g139,g142)
    c: InternalAlignment(g140,g142)
    c: InternalAlignment(g141,g142)
    c: InternalAlignment(g143,g142)
    c: InternalAlignment(g144,g142)
    c: Weight(g145) = 1
    c: Equal(g145,g146)
    c: Equal(g145,g147)
    c: InternalAlignment(g145,g148)
    c: InternalAlignment(g146,g148)
    c: InternalAlignment(g147,g148)
    c: InternalAlignment(g149,g148)
    c: InternalAlignment(g150,g148)
    c: Weight(g151) = 1
    c: Equal(g151,g152)
    c: Equal(g151,g153)
    c: InternalAlignment(g151,g154)
    c: InternalAlignment(g152,g154)
    c: InternalAlignment(g153,g154)
    c: InternalAlignment(g155,g154)
    c: InternalAlignment(g156,g154)
    c: Weight(g157) = 1
    c: Equal(g157,g158)
    c: Equal(g157,g159)
    c: InternalAlignment(g157,g160)
    c: InternalAlignment(g158,g160)
    c: InternalAlignment(g159,g160)
    c: InternalAlignment(g161,g160)
    c: InternalAlignment(g162,g160)
    c: Block(g160)
    c: Block(g154)
    c: Block(g148)
    c: Block(g142)
    c: Coincident(g163,g37)
    c: Coincident(g163,g160)
    c: Coincident(g164,g160)
    c: Coincident(g164,g154)
    c: Horizontal(g164)
    c: Coincident(g165,g154)
    c: Coincident(g165,g37)
    c: Vertical(g165)
    c: Coincident(g166,g31)
    c: Coincident(g166,g148)
    c: Vertical(g166)
    c: Coincident(g167,g148)
    c: Coincident(g167,g142)
    c: Horizontal(g167)
    c: Coincident(g168,g142)
    c: Coincident(g168,g31)
    c: Weight(g169) = 1
    c: Equal(g169,g170)
    c: Equal(g169,g171)
    c: InternalAlignment(g169,g172)
    c: InternalAlignment(g170,g172)
    c: InternalAlignment(g171,g172)
    c: InternalAlignment(g173,g172)
    c: InternalAlignment(g174,g172)
    c: Weight(g175) = 1
    c: Equal(g175,g176)
    c: Equal(g175,g177)
    c: InternalAlignment(g175,g178)
    c: InternalAlignment(g176,g178)
    c: InternalAlignment(g177,g178)
    c: InternalAlignment(g179,g178)
    c: InternalAlignment(g180,g178)
    c: Weight(g181) = 1
    c: Equal(g181,g182)
    c: Equal(g181,g183)
    c: InternalAlignment(g181,g184)
    c: InternalAlignment(g182,g184)
    c: InternalAlignment(g183,g184)
    c: InternalAlignment(g185,g184)
    c: InternalAlignment(g186,g184)
    c: Weight(g187) = 1
    c: Equal(g187,g188)
    c: Equal(g187,g189)
    c: InternalAlignment(g187,g190)
    c: InternalAlignment(g188,g190)
    c: InternalAlignment(g189,g190)
    c: InternalAlignment(g191,g190)
    c: InternalAlignment(g192,g190)
    c: Block(g190)
    c: Block(g184)
    c: Block(g178)
    c: Block(g172)
    c: Coincident(g193,g190)
    c: Coincident(g193,g184)
    c: Horizontal(g193)
    c: Coincident(g194,g184)
    c: Coincident(g194,g19)
    c: Vertical(g194)
    c: Coincident(g195,g25)
    c: Coincident(g195,g178)
    c: Vertical(g195)
    c: Coincident(g196,g178)
    c: Coincident(g196,g172)
    c: Horizontal(g196)
    c: Coincident(g197,g172)
    c: Coincident(g197,g25)
    c: Coincident(g198,g19)
    c: Weight(g199) = 1
    c: Equal(g199,g200)
    c: Equal(g199,g201)
    c: InternalAlignment(g199,g202)
    c: InternalAlignment(g200,g202)
    c: InternalAlignment(g201,g202)
    c: InternalAlignment(g203,g202)
    c: InternalAlignment(g204,g202)
    c: Weight(g205) = 1
    c: Equal(g205,g206)
    c: Equal(g205,g207)
    c: InternalAlignment(g205,g208)
    c: InternalAlignment(g206,g208)
    c: InternalAlignment(g207,g208)
    c: InternalAlignment(g209,g208)
    c: InternalAlignment(g210,g208)
    c: Block(g208)
    c: Block(g202)
    c: Coincident(g211,g208)
    c: Coincident(g211,g43)
    c: Coincident(g212,g43)
    c: Coincident(g212,g202)
    c: Coincident(g213,g202)
    c: Coincident(g213,g208)
    c: Vertical(g213)
    c: Weight(g214) = 1
    c: Equal(g214,g215)
    c: Equal(g214,g216)
    c: InternalAlignment(g214,g217)
    c: InternalAlignment(g215,g217)
    c: InternalAlignment(g216,g217)
    c: InternalAlignment(g218,g217)
    c: InternalAlignment(g219,g217)
    c: Weight(g220) = 1
    c: Equal(g220,g221)
    c: Equal(g220,g222)
    c: InternalAlignment(g220,g223)
    c: InternalAlignment(g221,g223)
    c: InternalAlignment(g222,g223)
    c: InternalAlignment(g224,g223)
    c: InternalAlignment(g225,g223)
    c: Block(g223)
    c: Block(g217)
    c: Coincident(g226,g217)
    c: Coincident(g226,g49)
    c: Coincident(g227,g49)
    c: Coincident(g227,g223)
    c: Coincident(g228,g223)
    c: Coincident(g228,g217)
    c: Vertical(g228)
    c: Horizontal(g229)
    c: Block(g229)
    c: Vertical(g230)
    c: Block(g230)
    c: Block(g231)
    c: Weight(g232) = 1
    c: Equal(g232,g233)
    c: Equal(g232,g234)
    c: InternalAlignment(g232,g235)
    c: InternalAlignment(g233,g235)
    c: InternalAlignment(g234,g235)
    c: InternalAlignment(g236,g235)
    c: InternalAlignment(g237,g235)
    c: Weight(g238) = 1
    c: Equal(g238,g239)
    c: Equal(g238,g240)
    c: InternalAlignment(g238,g241)
    c: InternalAlignment(g239,g241)
    c: InternalAlignment(g240,g241)
    c: InternalAlignment(g242,g241)
    c: InternalAlignment(g243,g241)
    c: Weight(g244) = 1
    c: Equal(g244,g245)
    c: Equal(g244,g246)
    c: InternalAlignment(g244,g247)
    c: InternalAlignment(g245,g247)
    c: InternalAlignment(g246,g247)
    c: InternalAlignment(g248,g247)
    c: InternalAlignment(g249,g247)
    c: Weight(g250) = 1
    c: Equal(g250,g251)
    c: Equal(g250,g252)
    c: InternalAlignment(g250,g253)
    c: InternalAlignment(g251,g253)
    c: InternalAlignment(g252,g253)
    c: InternalAlignment(g254,g253)
    c: InternalAlignment(g255,g253)
    c: Block(g235)
    c: Block(g241)
    c: Block(g247)
    c: Block(g253)
    c: Coincident(g256,g241)
    c: Coincident(g256,g235)
    c: Horizontal(g256)
    c: Block(g198)
    c: Weight(g257) = 1
    c: Equal(g257,g258)
    c: Equal(g257,g259)
    c: InternalAlignment(g257,g260)
    c: InternalAlignment(g258,g260)
    c: InternalAlignment(g259,g260)
    c: InternalAlignment(g261,g260)
    c: InternalAlignment(g262,g260)
    c: Weight(g263) = 1
    c: Equal(g263,g264)
    c: Equal(g263,g265)
    c: InternalAlignment(g263,g266)
    c: InternalAlignment(g264,g266)
    c: InternalAlignment(g265,g266)
    c: InternalAlignment(g267,g266)
    c: InternalAlignment(g268,g266)
    c: Weight(g269) = 1
    c: Equal(g269,g270)
    c: Equal(g269,g271)
    c: InternalAlignment(g269,g272)
    c: InternalAlignment(g270,g272)
    c: InternalAlignment(g271,g272)
    c: InternalAlignment(g273,g272)
    c: InternalAlignment(g274,g272)
    c: Weight(g275) = 1
    c: Equal(g275,g276)
    c: Equal(g275,g277)
    c: InternalAlignment(g275,g278)
    c: InternalAlignment(g276,g278)
    c: InternalAlignment(g277,g278)
    c: InternalAlignment(g279,g278)
    c: InternalAlignment(g280,g278)
    c: Block(g260)
    c: Block(g266)
    c: Block(g272)
    c: Block(g278)
    c: Coincident(g281,g272)
    c: Coincident(g281,g278)
    c: Horizontal(g281)
    c: Coincident(g282,g278)
    c: Coincident(g282,g260)
    c: Vertical(g282)
    c: Coincident(g283,g260)
    c: Coincident(g283,g266)
    c: Coincident(g284,g266)
    c: Coincident(g284,g272)
    c: Vertical(g284)
    c: Weight(g285) = 1
    c: Equal(g285,g286)
    c: Equal(g285,g287)
    c: InternalAlignment(g285,g288)
    c: InternalAlignment(g286,g288)
    c: InternalAlignment(g287,g288)
    c: InternalAlignment(g289,g288)
    c: InternalAlignment(g290,g288)
    c: Weight(g291) = 1
    c: Equal(g291,g292)
    c: Equal(g291,g293)
    c: InternalAlignment(g291,g294)
    c: InternalAlignment(g292,g294)
    c: InternalAlignment(g293,g294)
    c: InternalAlignment(g295,g294)
    c: InternalAlignment(g296,g294)
    c: Weight(g297) = 1
    c: Equal(g297,g298)
    c: Equal(g297,g299)
    c: InternalAlignment(g297,g300)
    c: InternalAlignment(g298,g300)
    c: InternalAlignment(g299,g300)
    c: InternalAlignment(g301,g300)
    c: InternalAlignment(g302,g300)
    c: Block(g300)
    c: Block(g294)
    c: Block(g288)
    c: Coincident(g303,g294)
    c: Coincident(g303,g288)
    c: Coincident(g304,g288)
    c: Coincident(g304,g300)
    c: Vertical(g304)
    c: Coincident(g305,g300)
    c: Coincident(g305,g294)
    c: Horizontal(g305)
    c: Weight(g306) = 1
    c: Equal(g306,g307)
    c: InternalAlignment(g306,g308)
    c: InternalAlignment(g307,g308)
    c: InternalAlignment(g309,g308)
    c: InternalAlignment(g310,g308)
    c: Weight(g311) = 1
    c: Equal(g311,g312)
    c: Equal(g311,g313)
    c: InternalAlignment(g311,g314)
    c: InternalAlignment(g312,g314)
    c: InternalAlignment(g313,g314)
    c: InternalAlignment(g315,g314)
    c: InternalAlignment(g316,g314)
    c: Weight(g317) = 1
    c: Equal(g317,g318)
    c: Equal(g317,g319)
    c: InternalAlignment(g317,g320)
    c: InternalAlignment(g318,g320)
    c: InternalAlignment(g319,g320)
    c: InternalAlignment(g321,g320)
    c: InternalAlignment(g322,g320)
    c: Equal(g323,g324)
    c: Equal(g323,g325)
    c: InternalAlignment(g323,g326)
    c: InternalAlignment(g324,g326)
    c: InternalAlignment(g325,g326)
    c: InternalAlignment(g327,g326)
    c: InternalAlignment(g328,g326)
    c: Block(g314)
    c: Block(g320)
    c: Block(g326)
    c: Block(g308)
FEATURE [Sketcher::SketchObject] Sketch001
  FullyConstrained = true
  MapMode = 4
  Placement = pos=(0,0,0) rot=(0.57735,0.57735,0.57735;2.0944rad)
  Support = -> [Sketch]
  sketch-geometry (46):
    g0: BSplineCurve PolesCount=3 KnotsCount=2 Degree=2 IsPeriodic=0
    g1: ArcOfCircle CenterX=73.1223 CenterY=-32.291 CenterZ=0 NormalX=0 NormalY=0 NormalZ=1 AngleXU=0 Radius=13 StartAngle=5.92268 EndAngle=9.06428
    g2: ArcOfCircle CenterX=66.7816 CenterY=-49.1439 CenterZ=0 NormalX=0 NormalY=0 NormalZ=1 AngleXU=0 Radius=13 StartAngle=2.78068 EndAngle=5.92131
    g3: ArcOfCircle CenterX=55.9263 CenterY=-78.1807 CenterZ=0 NormalX=0 NormalY=0 NormalZ=1 AngleXU=0 Radius=13 StartAngle=5.92268 EndAngle=9.06428
    g4: ArcOfCircle CenterX=49.5884 CenterY=-95.0342 CenterZ=0 NormalX=0 NormalY=0 NormalZ=1 AngleXU=0 Radius=13 StartAngle=2.78068 EndAngle=5.92131
    g5: ArcOfCircle CenterX=38.7206 CenterY=-124.067 CenterZ=0 NormalX=0 NormalY=0 NormalZ=1 AngleXU=0 Radius=13 StartAngle=5.92268 EndAngle=9.06428
    g6: ArcOfCircle CenterX=32.3875 CenterY=-140.92 CenterZ=0 NormalX=0 NormalY=0 NormalZ=1 AngleXU=0 Radius=13 StartAngle=2.78068 EndAngle=5.92131
    g7: ArcOfCircle CenterX=21.4715 CenterY=-169.934 CenterZ=0 NormalX=0 NormalY=0 NormalZ=1 AngleXU=0 Radius=13 StartAngle=5.92268 EndAngle=9.06428
    g8: ArcOfCircle CenterX=15.1336 CenterY=-186.787 CenterZ=0 NormalX=0 NormalY=0 NormalZ=1 AngleXU=0 Radius=13 StartAngle=2.78068 EndAngle=5.92131
    g9-g12: Circle x4 (B-spline internal-alignment scaffolding for g13; pole/knot coordinates omitted)
    g13: BSplineCurve PolesCount=4 KnotsCount=2 Degree=3 IsPeriodic=0
    g14: GeomPoint X=28.8094 Y=-19.0875 Z=0
    g15: GeomPoint X=47.0443 Y=-50.4712 Z=0
    g16: Circle CenterX=53.5586 CenterY=-23.2695 CenterZ=0 NormalX=0 NormalY=0 NormalZ=1 AngleXU=0 Radius=3.24518
    g17: Circle CenterX=-195.441 CenterY=-127.082 CenterZ=0 NormalX=0 NormalY=0 NormalZ=1 AngleXU=0 Radius=1
    g18: Circle CenterX=-8.24091 CenterY=-197.481 CenterZ=0 NormalX=0 NormalY=0 NormalZ=1 AngleXU=0 Radius=1
    g19: Circle CenterX=12.8789 CenterY=-141.321 CenterZ=0 NormalX=0 NormalY=0 NormalZ=1 AngleXU=0 Radius=1
    g20: BSplineCurve PolesCount=3 KnotsCount=2 Degree=2 IsPeriodic=0
    g21: GeomPoint X=-195.441 Y=-127.082 Z=0
    g22: GeomPoint X=12.8789 Y=-141.321 Z=0
    g23: Circle CenterX=-12.8016 CenterY=-179.036 CenterZ=0 NormalX=0 NormalY=0 NormalZ=1 AngleXU=0 Radius=10.5072
    g24: Circle CenterX=0.933922 CenterY=-166.43 CenterZ=0 NormalX=0 NormalY=0 NormalZ=1 AngleXU=0 Radius=3.26661
    g25: Circle CenterX=-33.5518 CenterY=-176.44 CenterZ=0 NormalX=0 NormalY=0 NormalZ=1 AngleXU=0 Radius=5.64388
    g26: Circle CenterX=-47.2366 CenterY=-173.859 CenterZ=0 NormalX=0 NormalY=0 NormalZ=1 AngleXU=0 Radius=3.01653
    g27: Circle CenterX=-56.2595 CenterY=-171.456 CenterZ=0 NormalX=0 NormalY=0 NormalZ=1 AngleXU=0 Radius=2.12826
    g28: ArcOfCircle CenterX=51.2151 CenterY=-198.473 CenterZ=0 NormalX=0 NormalY=0 NormalZ=1 AngleXU=0 Radius=20 StartAngle=2.78189 EndAngle=4.35269
    g29: LineSegment StartX=32.4951 StartY=-191.433 StartZ=0 EndX=94.6578 EndY=-26.1352 EndZ=0
    g30: LineSegment StartX=43.1192 StartY=-220.001 StartZ=0 EndX=-196.497 EndY=-129.89 EndZ=0
    g31: LineSegment StartX=43.1192 StartY=-220.001 StartZ=0 EndX=44.1752 EndY=-217.193 EndZ=0
    g32: LineSegment StartX=117.223 StartY=-19.0875 StartZ=0 EndX=117.223 EndY=-16.0875 EndZ=0
    g33: LineSegment StartX=117.223 StartY=-16.0875 StartZ=0 EndX=17.2232 EndY=-16.0875 EndZ=0
    g34: LineSegment StartX=17.2232 StartY=-16.0875 StartZ=0 EndX=17.2232 EndY=-19.0875 EndZ=0
    g35: LineSegment StartX=28.8094 StartY=-19.0875 StartZ=0 EndX=17.2232 EndY=-19.0875 EndZ=0
    g36: LineSegment StartX=47.0443 StartY=-50.4712 StartZ=0 EndX=12.8789 EndY=-141.321 EndZ=0
    g37: LineSegment StartX=-195.441 StartY=-127.082 StartZ=0 EndX=-196.497 EndY=-129.89 EndZ=0
    g38: LineSegment StartX=85.2866 StartY=-36.8766 StartZ=0 EndX=78.9396 EndY=-53.7463 EndZ=0
    g39: LineSegment StartX=60.9579 StartY=-27.7053 StartZ=0 EndX=54.6191 EndY=-44.5532 EndZ=0
    g40: LineSegment StartX=68.0907 StartY=-82.7664 StartZ=0 EndX=61.7465 EndY=-99.6365 EndZ=0
    g41: LineSegment StartX=43.7619 StartY=-73.595 StartZ=0 EndX=37.426 EndY=-90.4435 EndZ=0
    g42: LineSegment StartX=50.885 StartY=-128.652 StartZ=0 EndX=44.5456 EndY=-145.522 EndZ=0
    g43: LineSegment StartX=26.5562 StartY=-119.481 StartZ=0 EndX=20.2251 EndY=-136.329 EndZ=0
    g44: LineSegment StartX=9.3071 StartY=-165.349 StartZ=0 EndX=2.97115 EndY=-182.197 EndZ=0
    g45: LineSegment StartX=33.6358 StartY=-174.52 StartZ=0 EndX=27.2917 EndY=-191.39 EndZ=0
  constraints (71):
    c: Block(g0)
    c: Block(g1)
    c: Block(g2)
    c: Block(g4)
    c: Block(g3)
    c: Block(g6)
    c: Block(g5)
    c: Block(g8)
    c: Block(g7)
    c: Weight(g9) = 1
    c: Equal(g9,g10)
    c: Equal(g9,g11)
    c: Equal(g9,g12)
    c: InternalAlignment(g9-g12 -> g13) x4
    c: InternalAlignment(g14,g13)
    c: InternalAlignment(g15,g13)
    c: Block(g16)
    c: Weight(g17) = 1
    c: Equal(g17,g18)
    c: Equal(g17,g19)
    c: InternalAlignment(g17,g20)
    c: InternalAlignment(g18,g20)
    c: InternalAlignment(g19,g20)
    c: InternalAlignment(g21,g20)
    c: InternalAlignment(g22,g20)
    c: Block(g20)
    c: Block(g23)
    c: Block(g24)
    c: Block(g25)
    c: Block(g26)
    c: Block(g27)
    c: Block(g28)
    c: Coincident(g29,g28)
    c: Coincident(g29,g0)
    c: Block(g13)
    c: Coincident(g31,g30)
    c: Coincident(g31,g28)
    c: Block(g31)
    c: Coincident(g32,g0)
    c: Vertical(g32)
    c: Coincident(g33,g32)
    c: Horizontal(g33)
    c: Coincident(g34,g33)
    c: Vertical(g34)
    c: Block(g33)
    c: Coincident(g35,g13)
    c: Coincident(g35,g34)
    c: Horizontal(g35)
    c: Coincident(g36,g13)
    c: Coincident(g36,g20)
    c: Coincident(g37,g20)
    c: Coincident(g37,g30)
    c: Block(g30)
    c: Coincident(g38,g1)
    c: Coincident(g38,g2)
    c: Coincident(g39,g1)
    c: Coincident(g39,g2)
    c: Coincident(g40,g3)
    c: Coincident(g40,g4)
    c: Coincident(g41,g3)
    c: Coincident(g41,g4)
    c: Coincident(g42,g5)
    c: Coincident(g42,g6)
    c: Coincident(g43,g5)
    c: Coincident(g43,g6)
    c: Coincident(g44,g7)
    c: Coincident(g44,g8)
    c: Coincident(g45,g7)
    c: Coincident(g45,g8)
    c: Distance(g30) = 256
    c: Distance(g33) = 100
FEATURE [Part::Extrusion] Extrude002
  Base = -> Sketch001
  Dir = (1,0,0)
  DirMode = 2
  FaceMakerClass = Part::FaceMakerBullseye
  LengthFwd = 8
  LengthRev = 0
  Solid = true
  Symmetric = false
FEATURE [Sketcher::SketchObject] Sketch002
  FullyConstrained = true
  sketch-geometry (20):
    g0: LineSegment StartX=-2.77179 StartY=-200.304 StartZ=0 EndX=5.22821 EndY=-200.304 EndZ=0
    g1: LineSegment StartX=5.22821 StartY=-200.304 StartZ=0 EndX=5.22821 EndY=-197.304 EndZ=0
    g2: LineSegment StartX=-2.77179 StartY=-200.304 StartZ=0 EndX=-2.77179 EndY=-197.304 EndZ=0
    g3: LineSegment StartX=5.22821 StartY=-197.304 StartZ=0 EndX=8.22821 EndY=-197.304 EndZ=0
    g4: LineSegment StartX=-2.77179 StartY=-197.304 StartZ=0 EndX=-5.77179 EndY=-197.304 EndZ=0
    g5: LineSegment StartX=19.2282 StartY=-203.304 StartZ=0 EndX=19.2282 EndY=-206.304 EndZ=0
    g6: LineSegment StartX=-16.7718 StartY=-203.304 StartZ=0 EndX=-16.7718 EndY=-206.304 EndZ=0
    g7: LineSegment StartX=-16.7718 StartY=-206.304 StartZ=0 EndX=19.2282 EndY=-206.304 EndZ=0
    g8: Circle CenterX=-16.7718 CenterY=-203.304 CenterZ=0 NormalX=0 NormalY=0 NormalZ=1 AngleXU=0 Radius=1
    g9: Circle CenterX=-5.77179 CenterY=-203.304 CenterZ=0 NormalX=0 NormalY=0 NormalZ=1 AngleXU=0 Radius=1
    g10: Circle CenterX=-5.77179 CenterY=-197.304 CenterZ=0 NormalX=0 NormalY=0 NormalZ=1 AngleXU=0 Radius=1
    g11: BSplineCurve PolesCount=3 KnotsCount=2 Degree=2 IsPeriodic=0
    g12: GeomPoint X=-16.7718 Y=-203.304 Z=0
    g13: GeomPoint X=-5.77179 Y=-197.304 Z=0
    g14: Circle CenterX=19.2282 CenterY=-203.304 CenterZ=0 NormalX=0 NormalY=0 NormalZ=1 AngleXU=0 Radius=1
    g15: Circle CenterX=8.22821 CenterY=-203.304 CenterZ=0 NormalX=0 NormalY=0 NormalZ=1 AngleXU=0 Radius=1
    g16: Circle CenterX=8.22821 CenterY=-197.304 CenterZ=0 NormalX=0 NormalY=0 NormalZ=1 AngleXU=0 Radius=1
    g17: BSplineCurve PolesCount=3 KnotsCount=2 Degree=2 IsPeriodic=0
    g18: GeomPoint X=19.2282 Y=-203.304 Z=0
    g19: GeomPoint X=8.22821 Y=-197.304 Z=0
  constraints (41):
    c: Horizontal(g0)
    c: Distance(g0) = 8
    c: Coincident(g1,g0)
    c: Vertical(g1)
    c: Distance(g1) = 3
    c: Coincident(g2,g0)
    c: Vertical(g2)
    c: Distance(g2) = 3
    c: Coincident(g3,g1)
    c: Horizontal(g3)
    c: Distance(g3) = 3
    c: Coincident(g4,g2)
    c: Horizontal(g4)
    c: Distance(g4) = 3
    c: Vertical(g5)
    c: Vertical(g6)
    c: Coincident(g7,g6)
    c: Coincident(g7,g5)
    c: Weight(g8) = 1
    c: Equal(g8,g9)
    c: Equal(g8,g10)
    c: Coincident(g11,g4)
    c: InternalAlignment(g8,g11)
    c: InternalAlignment(g9,g11)
    c: InternalAlignment(g10,g11)
    c: InternalAlignment(g12,g11)
    c: InternalAlignment(g13,g11)
    c: Coincident(g17,g5)
    c: Weight(g14) = 1
    c: Equal(g14,g15)
    c: Equal(g14,g16)
    c: Coincident(g17,g3)
    c: InternalAlignment(g14,g17)
    c: InternalAlignment(g15,g17)
    c: InternalAlignment(g16,g17)
    c: InternalAlignment(g18,g17)
    c: InternalAlignment(g19,g17)
    c: Block(g7)
    c: Block(g17)
    c: Block(g11)
    c: Block(g6)
FEATURE [Part::Extrusion] Extrude003
  Base = -> Sketch002
  Dir = (0,0,1)
  DirMode = 2
  FaceMakerClass = Part::FaceMakerBullseye
  LengthFwd = 260
  LengthRev = 0
  Solid = true
  Symmetric = false
FEATURE [Part::Extrusion] Extrude
  Base = -> Sketch
  Dir = (0,0,1)
  DirMode = 2
  FaceMakerClass = Part::FaceMakerBullseye
  LengthFwd = 14
  LengthRev = 0
  Solid = true
  Symmetric = false
